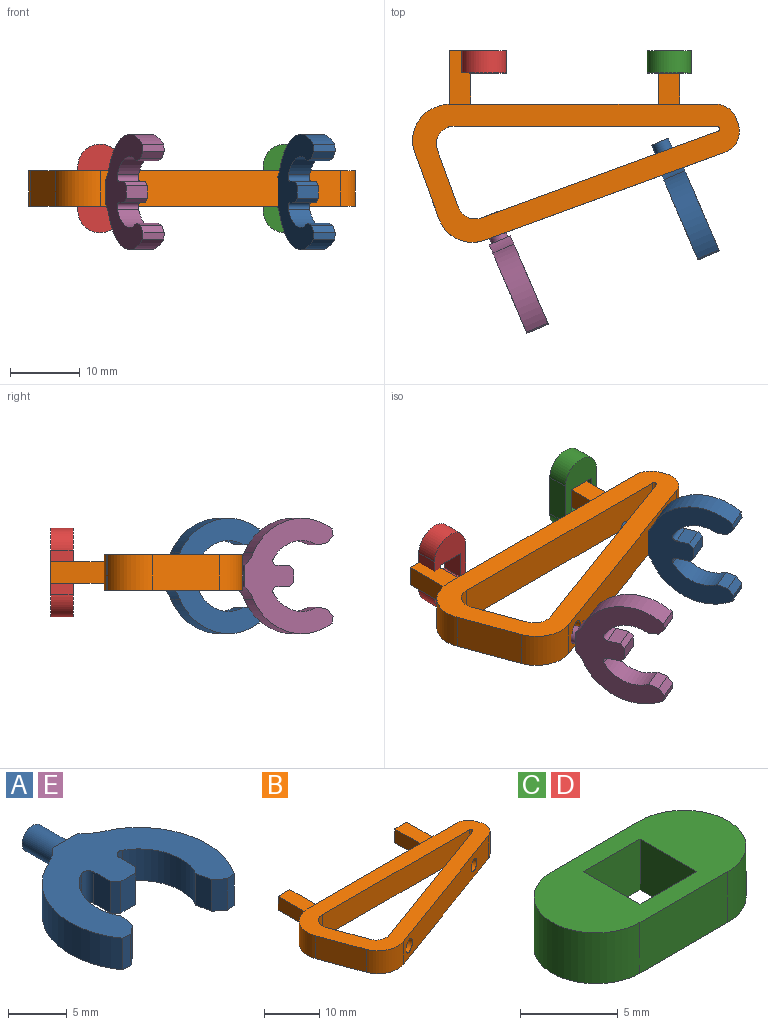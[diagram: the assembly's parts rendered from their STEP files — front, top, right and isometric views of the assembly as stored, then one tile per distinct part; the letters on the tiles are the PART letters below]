
ASSEMBLY  parts=5 mates=3
PART A: 24 faces, bbox 16.5x17.7x3.3 mm
  f0: cylinder r=5.08mm len=6.86mm, axis (0,0,-1), area 26.2mm2, adj f6,f7,f14,f20
  f1: cylinder r=8.26mm len=12.32mm, axis (0,0,-1), area 48.3mm2, adj f6,f7,f16,f22
  f2: plane 3.3x1.05mm, normal (0.64,-0.77,0), area 4.5mm2, adj f6,f7,f15,f17
  f3: cylinder r=5.08mm len=6.86mm, axis (0,0,-1), area 26.2mm2, adj f6,f7,f15,f21
  f4: plane 3.3x1.05mm, normal (-0.64,-0.77,0), area 4.5mm2, adj f6,f7,f14,f16
  f5: cylinder r=8.26mm len=12.32mm, axis (0,0,-1), area 48.3mm2, adj f6,f7,f17,f23
  f6: plane 16.51x13.77mm, normal (0,0,1), area 108.9mm2, adj f0,f1,f2,f3,f4,f5,f8,f9
  f7: plane 16.51x13.77mm, normal (0,0,-1), area 108.9mm2, adj f0,f1,f2,f3,f4,f5,f8,f9
  f8: plane 3.3x3.05mm, normal (0,1,0), area 5mm2, adj f6,f7,f11,f22,f23
  f9: plane 3.3x1.98mm, normal (1,0,0), area 6.5mm2, adj f6,f7,f18,f20
  f10: plane 3.3x1.98mm, normal (-1,0,0), area 6.5mm2, adj f6,f7,f19,f21
  f11: cylinder r=1.27mm len=3.94mm, axis (0,-1,0), area 31.4mm2, adj f8,f12
  f12: plane 2.54x2.54mm, normal (0,1,0), area 5.1mm2, adj f11
  f13: plane 3.3x1.78mm, normal (0,-1,0), area 5.9mm2, adj f6,f7,f18,f19
  f14: plane 3.3x1.58mm, normal (-0.98,-0.19,0), area 5.3mm2, adj f0,f4,f6,f7
  f15: plane 3.3x1.58mm, normal (0.98,-0.19,0), area 5.3mm2, adj f2,f3,f6,f7
  f16: plane 3.3x0.93mm, normal (0.13,-0.99,0), area 3.1mm2, adj f1,f4,f6,f7
  f17: plane 3.3x0.93mm, normal (-0.13,-0.99,0), area 3.1mm2, adj f2,f5,f6,f7
  f18: plane 3.3x0.64mm, normal (0.71,-0.71,0), area 3mm2, adj f6,f7,f9,f13
  f19: plane 3.3x0.64mm, normal (-0.71,-0.71,0), area 3mm2, adj f6,f7,f10,f13
  f20: cylinder r=0.64mm len=3.3mm, axis (0,0,-1), area 4.4mm2, adj f0,f6,f7,f9
  f21: cylinder r=0.64mm len=3.3mm, axis (0,0,-1), area 4.4mm2, adj f3,f6,f7,f10
  f22: cylinder r=5.08mm len=3.3mm, axis (0,0,1), area 7.5mm2, adj f1,f6,f7,f8
  f23: cylinder r=5.08mm len=3.3mm, axis (0,0,1), area 7.5mm2, adj f5,f6,f7,f8
PART B: 30 faces, bbox 46.8x27.4x5.1 mm
  f0: plane 7.62x3.05mm, normal (1,0,0), area 23.2mm2, adj f1,f16,f28,f29
  f1: plane 3.05x3.05mm, normal (0,1,0), area 9.3mm2, adj f0,f2,f28,f29
  f2: plane 7.62x3.05mm, normal (-1,0,0), area 23.2mm2, adj f1,f18,f28,f29
  f3: plane 7.62x3.05mm, normal (1,0,0), area 23.2mm2, adj f4,f16,f26,f27
  f4: plane 3.05x3.05mm, normal (0,1,0), area 9.3mm2, adj f3,f5,f26,f27
  f5: plane 7.62x3.05mm, normal (-1,0,0), area 23.2mm2, adj f4,f16,f26,f27
  f6: plane 34.44x12.59mm, normal (0.34,-0.94,0), area 175.1mm2, adj f7,f8,f20,f21,f22,f24
  f7: plane 46.84x19.83mm, normal (0,0,1), area 327.1mm2, adj f6,f9,f10,f11,f12,f13,f14,f15
  f8: plane 46.84x19.83mm, normal (0,0,-1), area 327.1mm2, adj f6,f9,f10,f11,f12,f13,f14,f15
  f9: plane 8.22x5.08mm, normal (0.94,0.34,0), area 44.5mm2, adj f7,f8,f10,f17
  f10: cylinder r=2.54mm len=5.08mm, axis (0,0,-1), area 24.8mm2, adj f7,f8,f9,f11
  f11: plane 37.68x5.08mm, normal (0,-1,0), area 191.4mm2, adj f7,f8,f10,f12
  f12: cylinder r=0.38mm len=5.08mm, axis (0,0,-1), area 5.4mm2, adj f7,f8,f11,f13
  f13: plane 33.94x12.41mm, normal (-0.34,0.94,0), area 172.4mm2, adj f7,f8,f12,f17,f21,f22
  f14: plane 5.08x0.35mm, normal (-0.34,0.94,0), area 1.9mm2, adj f7,f8,f18,f19
  f15: plane 9.54x5.08mm, normal (-0.94,-0.34,0), area 51.6mm2, adj f7,f8,f19,f20
  f16: plane 38.09x5.08mm, normal (0,1,0), area 174.9mm2, adj f0,f3,f5,f7,f8,f18,f25,f26
  f17: cylinder r=2.54mm len=5.08mm, axis (0,0,-1), area 20.3mm2, adj f7,f8,f9,f13
  f18: cylinder r=5.08mm len=5.08mm, axis (0,0,1), area 8.3mm2, adj f2,f7,f8,f14,f16
  f19: cylinder r=5.08mm len=6.52mm, axis (0,0,-1), area 40.5mm2, adj f7,f8,f14,f15
  f20: cylinder r=5.08mm len=6.52mm, axis (0,0,-1), area 40.5mm2, adj f6,f7,f8,f15
  f21: cylinder r=1.27mm len=3.85mm, axis (0.34,-0.94,0), area 25.3mm2, adj f6,f13
  f22: cylinder r=1.4mm len=3.94mm, axis (0.34,-0.94,0), area 27.9mm2, adj f6,f13
  f23: plane 5.08x0.77mm, normal (0.94,0.34,0), area 4.2mm2, adj f7,f8,f24,f25
  f24: cylinder r=3.17mm len=5.08mm, axis (0,0,1), area 25.3mm2, adj f6,f7,f8,f23
  f25: cylinder r=3.17mm len=5.08mm, axis (0,0,-1), area 19.7mm2, adj f7,f8,f16,f23
  f26: plane 7.62x3.05mm, normal (0,0,-1), area 23.2mm2, adj f3,f4,f5,f16
  f27: plane 7.62x3.05mm, normal (0,0,1), area 23.2mm2, adj f3,f4,f5,f16
  f28: plane 7.62x3.05mm, normal (0,0,1), area 23.2mm2, adj f0,f1,f2,f16
  f29: plane 7.62x3.05mm, normal (0,0,-1), area 23.2mm2, adj f0,f1,f2,f16
PART C: 10 faces, bbox 12.7x6.4x3.2 mm
  f0: plane 4.06x3.18mm, normal (0,-1,0), area 12.9mm2, adj f1,f5,f6,f7
  f1: plane 4.06x3.18mm, normal (-1,0,0), area 12.9mm2, adj f0,f2,f6,f7
  f2: plane 4.06x3.18mm, normal (0,1,0), area 12.9mm2, adj f1,f5,f6,f7
  f3: plane 6.35x3.18mm, normal (0,1,0), area 20.2mm2, adj f6,f7,f8,f9
  f4: plane 6.35x3.18mm, normal (0,-1,0), area 20.2mm2, adj f6,f7,f8,f9
  f5: plane 4.06x3.18mm, normal (1,0,0), area 12.9mm2, adj f0,f2,f6,f7
  f6: plane 12.7x6.35mm, normal (0,0,1), area 55.5mm2, adj f0,f1,f2,f3,f4,f5,f8,f9
  f7: plane 12.7x6.35mm, normal (0,0,-1), area 55.5mm2, adj f0,f1,f2,f3,f4,f5,f8,f9
  f8: cylinder r=3.17mm len=6.35mm, axis (0,0,-1), area 31.7mm2, adj f3,f4,f6,f7
  f9: cylinder r=3.17mm len=6.35mm, axis (0,0,1), area 31.7mm2, adj f3,f4,f6,f7
PART D: same geometry as C
PART E: same geometry as A
PLACE A rot(axis=(-0.2,0.96,0.2),92.3deg) t=(30.65,-25.46,2.03)mm
PLACE B at identity fixed
PLACE C rot(axis=(-0.58,0.58,0.58),120deg) t=(28.45,-3.18,2.54)mm
PLACE D rot(axis=(-0.58,0.58,0.58),120deg) t=(1.9,-3.18,2.54)mm
PLACE E rot(axis=(-0.2,0.96,0.2),92.3deg) t=(6.13,-35.97,2.03)mm
MATE fastened C.f6 <-> B.f4  axis (0,1,0) through (28.45,0,2.54)mm
MATE parallel A.f10 <-> B.f7  axis (0,0,1) through (31.02,-22.15,3.56)mm
MATE parallel E.f10 <-> B.f7  axis (0,0,1) through (6.51,-32.66,3.56)mm
